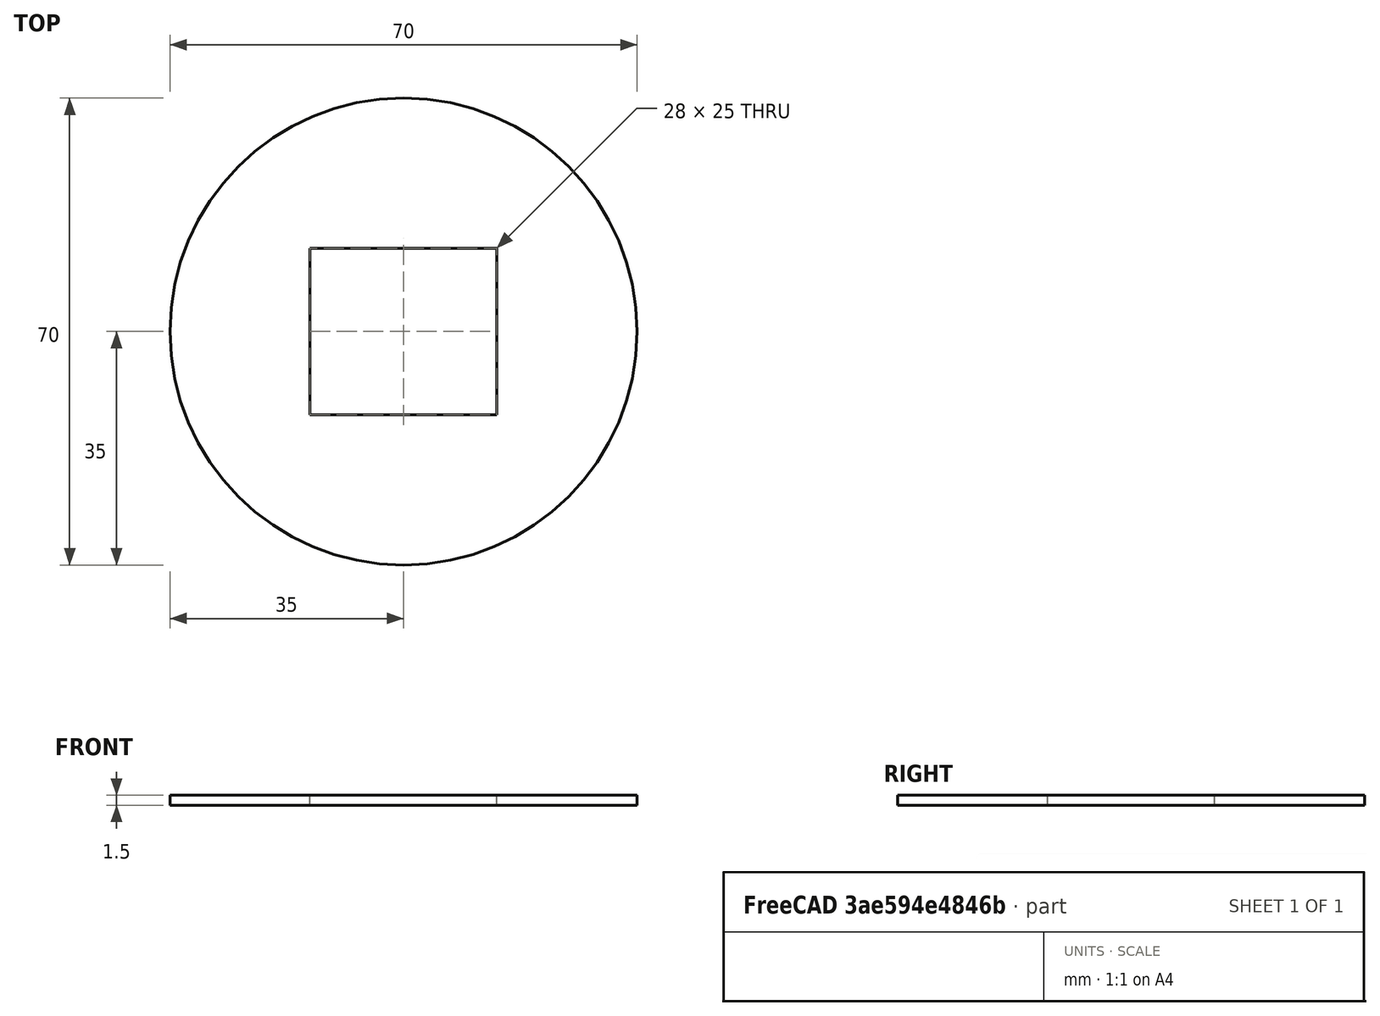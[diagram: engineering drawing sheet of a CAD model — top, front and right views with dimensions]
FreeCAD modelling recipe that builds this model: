
FCSTD DOCUMENT  (FreeCAD 0.14R3700 (Git))
Label: BR_PCB_mezzanine
License: CC-BY 3.0
LicenseURL: http://creativecommons.org/licenses/by/3.0/
objects: Sketcher::SketchObject×1, Part::Extrusion×1, Part::Feature×1
note: 3 computed .brp shape members not serialized (recipe doc carries the construction recipe); baked Part::Feature solids carry a one-line shape summary decoded from their .brp

FEATURE [Sketcher::SketchObject] Sketch  label="PCB_mezzanine"
  sketch-geometry (5):
    g0: Circle CenterX=0 CenterY=0 CenterZ=0 NormalX=0 NormalY=0 NormalZ=1 Radius=35
    g1: LineSegment StartX=-14 StartY=-12.5 StartZ=0 EndX=14 EndY=-12.5 EndZ=0
    g2: LineSegment StartX=14 StartY=-12.5 StartZ=0 EndX=14 EndY=12.5 EndZ=0
    g3: LineSegment StartX=14 StartY=12.5 StartZ=0 EndX=-14 EndY=12.5 EndZ=0
    g4: LineSegment StartX=-14 StartY=12.5 StartZ=0 EndX=-14 EndY=-12.5 EndZ=0
  constraints (14):
    c: Coincident(g0,g-1)
    c: Radius(g0) = 35
    c: Coincident(g1,g2)
    c: Coincident(g2,g3)
    c: Coincident(g3,g4)
    c: Coincident(g4,g1)
    c: Horizontal(g1)
    c: Horizontal(g3)
    c: Vertical(g2)
    c: Vertical(g4)
    c: Symmetric(g3,g2,g-2)
    c: Symmetric(g1,g3,g-1)
    c: DistanceX(g3) = -28
    c: DistanceY(g2) = 25
FEATURE [Part::Extrusion] Extrude
  Base = -> Sketch
  Dir = (0,0,1.5)
  Solid = true
FEATURE [Part::Feature] Extrude001  label="PCB_Mezzanine"
  shape: bbox 70 x 70 x 1.5 mm, 7 faces (baked)
